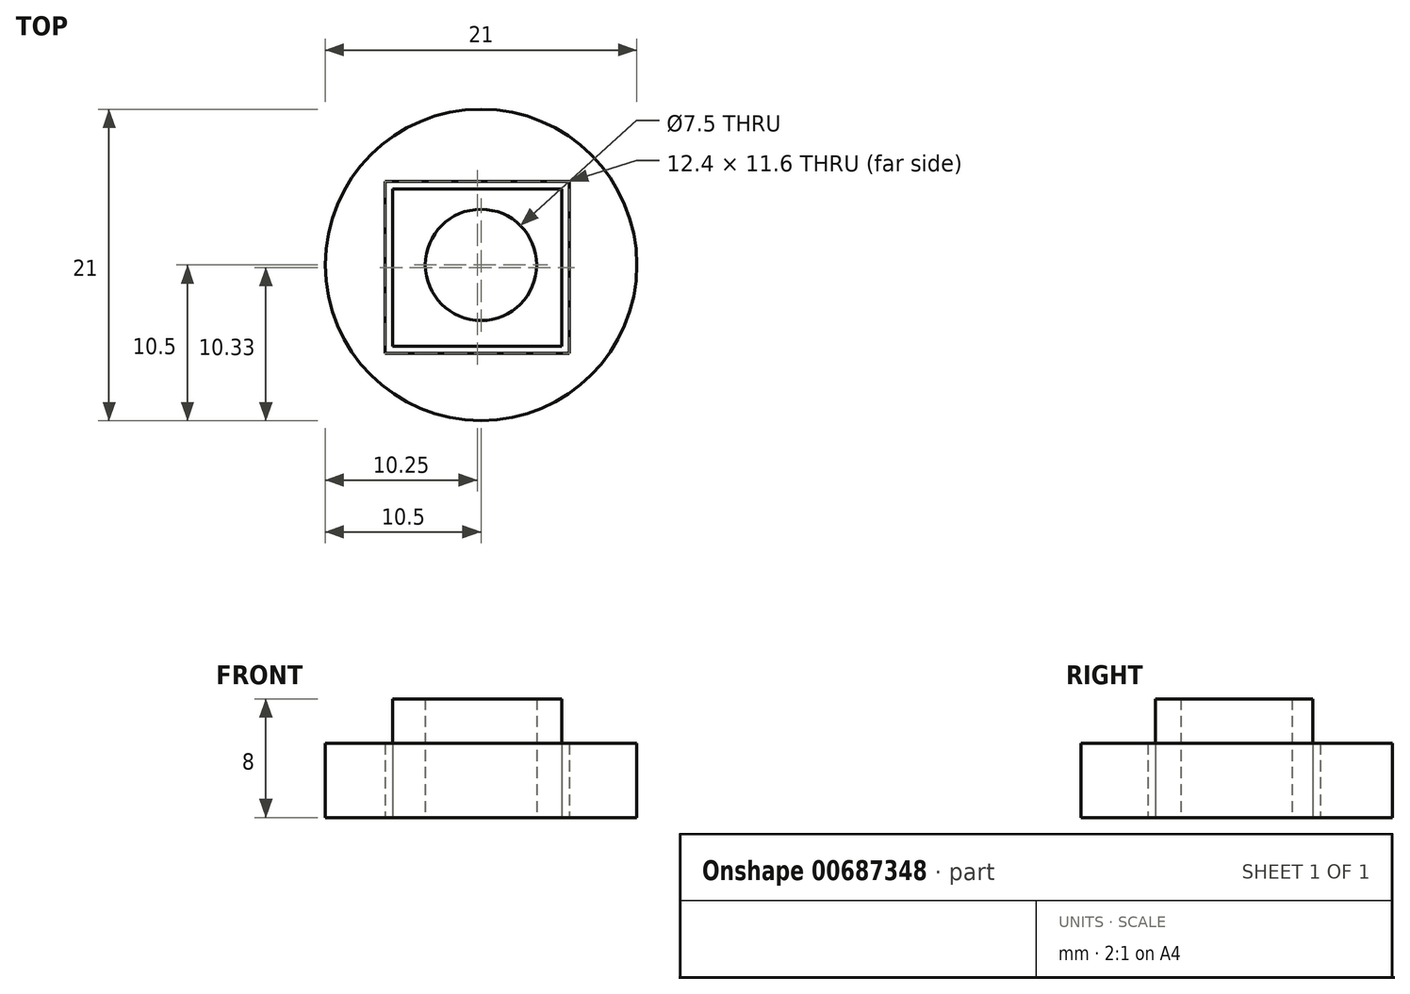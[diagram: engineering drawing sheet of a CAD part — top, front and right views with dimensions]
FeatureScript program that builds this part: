
annotation { "Feature Type Name" : "Feature", "Feature Type Description" : "" }
export const myFeature = defineFeature(function(context is Context, id is Id, definition is map)
    precondition{}
    {
        {
            var Q0;
            Q0=qCreatedBy(makeId("Top.planeOp"),FACE);
            var sketch = newSketch(context, id + "F0", { "sketchPlane" : qUnion([Q0])});
            skCircle(sketch, "E0", {"center": v(0, 0) * mm, "radius": 3.75 * mm});
            skLineSegment(sketch, "E1.bottom", {"start": v(-5.95, 5.13) * mm, "end": v(5.45, 5.13) * mm});
            skLineSegment(sketch, "E1.top", {"start": v(-5.95, -5.47) * mm, "end": v(5.45, -5.47) * mm});
            skLineSegment(sketch, "E1.left", {"start": v(-5.95, 5.13) * mm, "end": v(-5.95, -5.47) * mm});
            skLineSegment(sketch, "E1.right", {"start": v(5.45, 5.13) * mm, "end": v(5.45, -5.47) * mm});
            skSolve(sketch);
        }
        {
            var Q0;
            Q0=makeQuery(id+"F0.imprint","IMPRINT",FACE,{"disambiguationData":[TD([[makeQuery(id+"F0.imprint","IMPRINT",EDGE,{"derivedFrom":sQuery(id+"F0.wireOp",EDGE,"E0")}),-1.0]])]});
            extrude(context, id + "F1", {"entities" : qUnion([Q0]), "depth" : 8 * mm, "offsetDistance" : 25 * mm});
        }
        {
            var Q0;
            Q0=qCreatedBy(makeId("Top.planeOp"),FACE);
            var sketch = newSketch(context, id + "F2", { "sketchPlane" : qUnion([Q0])});
            skCircle(sketch, "E2", {"center": v(0, 0) * mm, "radius": 10.5 * mm});
            skLineSegment(sketch, "E3.bottom", {"start": v(-6.45, 5.63) * mm, "end": v(5.95, 5.63) * mm});
            skLineSegment(sketch, "E3.top", {"start": v(-6.45, -5.97) * mm, "end": v(5.95, -5.97) * mm});
            skLineSegment(sketch, "E3.left", {"start": v(-6.45, 5.63) * mm, "end": v(-6.45, -5.97) * mm});
            skLineSegment(sketch, "E3.right", {"start": v(5.95, 5.63) * mm, "end": v(5.95, -5.97) * mm});
            skSolve(sketch);
        }
        {
            var Q0;
            Q0=makeQuery(id+"F2.imprint","IMPRINT",FACE,{"disambiguationData":[TD([[makeQuery(id+"F2.imprint","IMPRINT",EDGE,{"derivedFrom":sQuery(id+"F2.wireOp",EDGE,"E2")}),1.0]])]});
            extrude(context, id + "F3", {"entities" : qUnion([Q0]), "depth" : 5 * mm, "offsetDistance" : 25 * mm});
        }
    });
